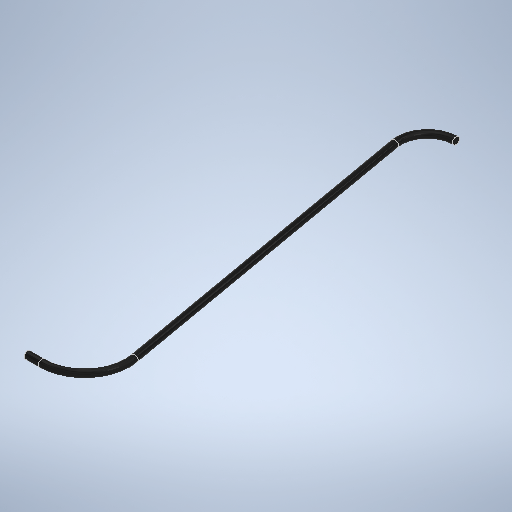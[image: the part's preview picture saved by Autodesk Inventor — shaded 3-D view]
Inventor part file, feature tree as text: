
AUTODESK INVENTOR PART (.ipt)
format: ipt  version: 2025.2 (Build 292293000, 293)  size: 277,504 bytes
history: native  units: mm
features: sketch x4, extrude x2, revolve x2, other x1
ambient origin geometry x8: Origin, YZ Plane, XZ Plane, XY Plane, X Axis, Y Axis, Z Axis, Center Point
bodies: Body1 (feature_tree)
feature tree (9):
  other  "ソリッド1"
  extrude  "押し出し1"  Depth=0.5mm
  revolve  "回転1"
  extrude  "押し出し2"  Depth=1.0mm TaperAngle=0.0deg
  revolve  "回転2"
  sketch  "スケッチ1"
  sketch  "スケッチ2"
  sketch  "スケッチ3"
  sketch  "スケッチ4"
